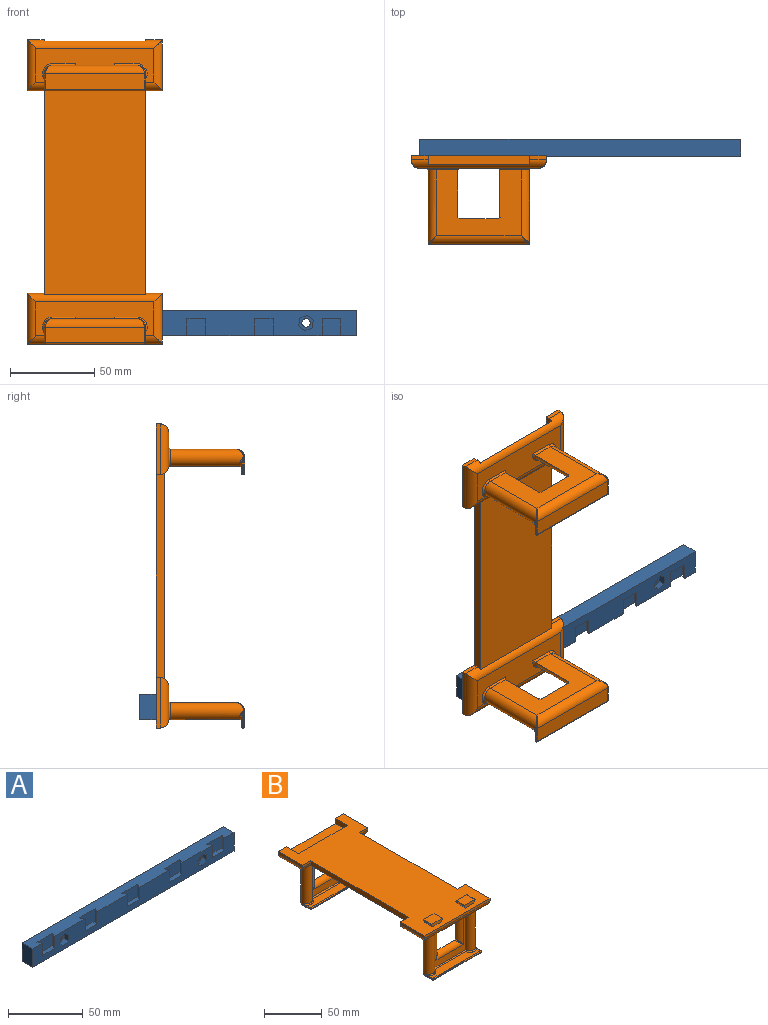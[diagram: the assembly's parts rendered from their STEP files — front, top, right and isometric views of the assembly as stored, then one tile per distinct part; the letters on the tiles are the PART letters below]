
ASSEMBLY  parts=2 mates=1
PART A: 42 faces, bbox 190x10x15 mm
  f0: plane 190x10mm, normal (0,0,1), area 1674.8mm2, adj f1,f2,f10,f13,f14,f15,f17,f18
  f1: plane 190x15mm, normal (0,-1,0), area 2189.1mm2, adj f0,f2,f3,f4,f5,f6,f7,f8
  f2: plane 15x10mm, normal (-1,0,0), area 150mm2, adj f0,f1,f3,f10
  f3: plane 190x10mm, normal (0,0,-1), area 1900mm2, adj f1,f2,f10,f24
  f4: plane 4.57x4mm, normal (-0.99,0,0.14), area 18.5mm2, adj f1,f5,f9,f12
  f5: plane 4.29x4mm, normal (-0.37,0,0.93), area 18.5mm2, adj f1,f4,f6,f12
  f6: plane 4x3.63mm, normal (0.62,0,0.79), area 18.5mm2, adj f1,f5,f7,f12
  f7: plane 4.57x4mm, normal (0.99,0,-0.14), area 18.5mm2, adj f1,f6,f8,f12
  f8: plane 4.29x4mm, normal (0.37,0,-0.93), area 18.5mm2, adj f1,f7,f9,f12
  f9: plane 4x3.63mm, normal (-0.62,0,-0.79), area 18.5mm2, adj f1,f4,f8,f12
  f10: plane 190x15mm, normal (0,1,0), area 2810.7mm2, adj f0,f2,f3,f11,f24,f31
  f11: cylinder r=2.5mm len=6mm, axis (0,1,0), area 94.2mm2, adj f10,f12
  f12: plane 9.14x8.58mm, normal (0,-1,0), area 35.8mm2, adj f4,f5,f6,f7,f8,f9,f11
  f13: plane 10x3.46mm, normal (-0.87,0.5,0), area 40mm2, adj f0,f1,f14,f16
  f14: plane 15x10mm, normal (0,-1,0), area 150mm2, adj f0,f13,f15,f16
  f15: plane 10x3.46mm, normal (0.87,0.5,0), area 40mm2, adj f0,f1,f14,f16
  f16: plane 15x3.46mm, normal (0,0,1), area 45mm2, adj f1,f13,f14,f15
  f17: plane 10x3.46mm, normal (0.87,0.5,0), area 40mm2, adj f0,f1,f19,f20
  f18: plane 10x3.46mm, normal (-0.87,0.5,0), area 40mm2, adj f0,f1,f19,f20
  f19: plane 15x10mm, normal (0,-1,0), area 150mm2, adj f0,f17,f18,f20
  f20: plane 15x3.46mm, normal (0,0,1), area 45mm2, adj f1,f17,f18,f19
  f21: plane 15x10mm, normal (0,-1,0), area 150mm2, adj f0,f22,f23,f41
  f22: plane 10x3.46mm, normal (0.87,0.5,0), area 40mm2, adj f0,f1,f21,f23
  f23: plane 15x3.46mm, normal (0,0,1), area 45mm2, adj f1,f21,f22,f41
  f24: plane 15x10mm, normal (1,0,0), area 150mm2, adj f0,f1,f3,f10
  f25: plane 4.57x4mm, normal (0.99,0,0.14), area 18.5mm2, adj f1,f26,f30,f32
  f26: plane 4.29x4mm, normal (0.37,0,0.93), area 18.5mm2, adj f1,f25,f27,f32
  f27: plane 4x3.63mm, normal (-0.62,0,0.79), area 18.5mm2, adj f1,f26,f28,f32
  f28: plane 4.57x4mm, normal (-0.99,0,-0.14), area 18.5mm2, adj f1,f27,f29,f32
  f29: plane 4.29x4mm, normal (-0.37,0,-0.93), area 18.5mm2, adj f1,f28,f30,f32
  f30: plane 4x3.63mm, normal (0.62,0,-0.79), area 18.5mm2, adj f1,f25,f29,f32
  f31: cylinder r=2.5mm len=6mm, axis (0,1,0), area 94.2mm2, adj f10,f32
  f32: plane 9.14x8.58mm, normal (0,-1,0), area 35.8mm2, adj f25,f26,f27,f28,f29,f30,f31
  f33: plane 10x3.46mm, normal (0.87,0.5,0), area 40mm2, adj f0,f1,f34,f36
  f34: plane 15x10mm, normal (0,-1,0), area 150mm2, adj f0,f33,f35,f36
  f35: plane 10x3.46mm, normal (-0.87,0.5,0), area 40mm2, adj f0,f1,f34,f36
  f36: plane 15x3.46mm, normal (0,0,1), area 45mm2, adj f1,f33,f34,f35
  f37: plane 10x3.46mm, normal (-0.87,0.5,0), area 40mm2, adj f0,f1,f39,f40
  f38: plane 10x3.46mm, normal (0.87,0.5,0), area 40mm2, adj f0,f1,f39,f40
  f39: plane 15x10mm, normal (0,-1,0), area 150mm2, adj f0,f37,f38,f40
  f40: plane 15x3.46mm, normal (0,0,1), area 45mm2, adj f1,f37,f38,f39
  f41: plane 10x3.46mm, normal (-0.87,0.5,0), area 40mm2, adj f0,f1,f21,f23
PART B: 135 faces, bbox 80.1x180.1x55.8 mm
  f0: plane 10x2.44mm, normal (0,1,0), area 24.4mm2, adj f3,f7,f12,f95
  f1: plane 10x2.44mm, normal (0,1,0), area 24.4mm2, adj f3,f23,f25,f87
  f2: plane 10x2.44mm, normal (0,-1,0), area 24.4mm2, adj f3,f5,f24,f88
  f3: plane 180x80mm, normal (0,0,1), area 10888mm2, adj f0,f1,f2,f5,f7,f11,f12,f13
  f4: plane 70x20mm, normal (0,0,-1), area 1077.8mm2, adj f86,f87,f88,f89,f97,f98,f99,f100
  f5: plane 121.41x5mm, normal (-1,0,0), area 601.2mm2, adj f2,f3,f6,f14,f88,f95
  f6: plane 121.41x60mm, normal (0,0,-1), area 7284.3mm2, adj f5,f7,f88,f95
  f7: plane 121.41x5mm, normal (1,0,0), area 601.2mm2, adj f0,f3,f6,f27,f88,f95
  f8: plane 58.6x8.3mm, normal (0,0,1), area 403.6mm2, adj f66,f70,f72,f121,f122,f123
  f9: plane 70x20mm, normal (0,0,-1), area 1077.8mm2, adj f93,f94,f95,f96,f109,f110,f111,f113
  f10: plane 41.08x40mm, normal (0,-1,0), area 453.2mm2, adj f73,f75,f90,f91,f92,f113,f122,f128
  f11: plane 30x2.44mm, normal (-1,0,0), area 73.3mm2, adj f3,f13,f14,f93
  f12: plane 30x2.44mm, normal (1,0,0), area 73.3mm2, adj f0,f3,f13,f96
  f13: plane 80x2.44mm, normal (0,-1,0), area 195.5mm2, adj f3,f11,f12,f94
  f14: plane 10x2.44mm, normal (0,1,0), area 24.4mm2, adj f3,f5,f11,f95
  f15: plane 60x5mm, normal (0,1,0), area 300mm2, adj f3,f21,f22,f23
  f16: plane 9.3x0.52mm, normal (-1,0,0), area 4.8mm2, adj f61,f65,f66,f75
  f17: plane 9.3x0.52mm, normal (1,0,0), area 4.8mm2, adj f63,f69,f72,f73
  f18: plane 50x39mm, normal (0,1,0), area 1226mm2, adj f73,f75,f76,f90,f91,f92,f109,f125
  f19: plane 58.6x9.3mm, normal (0,0,-1), area 545mm2, adj f61,f63,f64,f76
  f20: plane 58.6x0.52mm, normal (0,-1,0), area 30.5mm2, adj f64,f65,f69,f70
  f21: plane 15x5mm, normal (1,0,0), area 74.4mm2, adj f3,f15,f22,f26,f87
  f22: plane 60x14.3mm, normal (0,0,1), area 857.8mm2, adj f15,f21,f23,f87
  f23: plane 15x5mm, normal (-1,0,0), area 74.4mm2, adj f1,f3,f15,f22,f87
  f24: plane 30x2.44mm, normal (-1,0,0), area 73.3mm2, adj f2,f3,f26,f89
  f25: plane 30x2.44mm, normal (1,0,0), area 73.3mm2, adj f1,f3,f27,f86
  f26: plane 10x2.44mm, normal (0,1,0), area 24.4mm2, adj f3,f21,f24,f87
  f27: plane 10x2.44mm, normal (0,-1,0), area 24.4mm2, adj f3,f7,f25,f88
  f28: plane 41.08x40mm, normal (0,-1,0), area 453.2mm2, adj f78,f79,f83,f84,f85,f100,f104,f117
  f29: plane 50x39mm, normal (0,1,0), area 1226mm2, adj f78,f79,f81,f83,f84,f85,f97,f108
  f30: plane 58.6x8.3mm, normal (0,0,1), area 403.6mm2, adj f51,f57,f60,f116,f117,f118
  f31: plane 9.3x0.52mm, normal (-1,0,0), area 4.8mm2, adj f54,f58,f60,f78
  f32: plane 9.3x0.52mm, normal (1,0,0), area 4.8mm2, adj f49,f51,f52,f79
  f33: plane 58.6x9.3mm, normal (0,0,-1), area 545mm2, adj f49,f53,f54,f81
  f34: plane 58.6x0.52mm, normal (0,-1,0), area 30.5mm2, adj f52,f53,f57,f58
  f35: plane 10x2.54mm, normal (-0.87,0,-0.5), area 29.3mm2, adj f3,f39,f40,f41
  f36: plane 10x2.54mm, normal (0.87,0,-0.5), area 29.3mm2, adj f3,f37,f40,f41
  f37: cylinder r=0.5mm len=10mm, axis (0,1,0), area 10.5mm2, adj f36,f38,f40,f41
  f38: plane 12.67x10mm, normal (0,0,1), area 126.7mm2, adj f37,f39,f40,f41
  f39: cylinder r=0.5mm len=10mm, axis (0,1,0), area 10.5mm2, adj f35,f38,f40,f41
  f40: plane 13.67x3.29mm, normal (0,-1,0), area 40.8mm2, adj f3,f35,f36,f37,f38,f39
  f41: plane 13.67x3.29mm, normal (0,1,0), area 40.8mm2, adj f3,f35,f36,f37,f38,f39
  f42: plane 10x2.54mm, normal (-0.87,0,-0.5), area 29.3mm2, adj f3,f46,f47,f48
  f43: plane 10x2.54mm, normal (0.87,0,-0.5), area 29.3mm2, adj f3,f44,f47,f48
  f44: cylinder r=0.5mm len=10mm, axis (0,1,0), area 10.5mm2, adj f43,f45,f47,f48
  f45: plane 12.67x10mm, normal (0,0,1), area 126.7mm2, adj f44,f46,f47,f48
  f46: cylinder r=0.5mm len=10mm, axis (0,1,0), area 10.5mm2, adj f42,f45,f47,f48
  f47: plane 13.67x3.29mm, normal (0,-1,0), area 40.8mm2, adj f3,f42,f43,f44,f45,f46
  f48: plane 13.67x3.29mm, normal (0,1,0), area 40.8mm2, adj f3,f42,f43,f44,f45,f46
  f49: cylinder r=0.7mm len=9.3mm, axis (0,1,0), area 10.2mm2, adj f32,f33,f50,f82
  f50: sphere r=0.7mm, area 0.8mm2, adj f49,f52,f53
  f51: cylinder r=0.7mm len=9.3mm, axis (0,-1,0), area 7.9mm2, adj f30,f32,f55,f115
  f52: cylinder r=0.7mm len=0.7mm, axis (0,0,1), area 0.6mm2, adj f32,f34,f50,f55
  f53: cylinder r=0.7mm len=58.6mm, axis (1,0,0), area 64.4mm2, adj f33,f34,f50,f56
  f54: cylinder r=0.7mm len=9.3mm, axis (0,1,0), area 10.2mm2, adj f31,f33,f56,f80
  f55: sphere r=0.7mm, area 0.8mm2, adj f51,f52,f57
  f56: sphere r=0.7mm, area 0.8mm2, adj f53,f54,f58
  f57: cylinder r=0.7mm len=58.6mm, axis (-1,0,0), area 64.4mm2, adj f30,f34,f55,f59
  f58: cylinder r=0.7mm len=0.7mm, axis (0,0,-1), area 0.6mm2, adj f31,f34,f56,f59
  f59: sphere r=0.7mm, area 0.8mm2, adj f57,f58,f60
  f60: cylinder r=0.7mm len=9.3mm, axis (0,-1,0), area 7.9mm2, adj f30,f31,f59,f119
  f61: cylinder r=0.7mm len=9.3mm, axis (0,1,0), area 10.2mm2, adj f16,f19,f62,f77
  f62: sphere r=0.7mm, area 0.8mm2, adj f61,f64,f65
  f63: cylinder r=0.7mm len=9.3mm, axis (0,1,0), area 10.2mm2, adj f17,f19,f67,f74
  f64: cylinder r=0.7mm len=58.6mm, axis (-1,0,0), area 64.4mm2, adj f19,f20,f62,f67
  f65: cylinder r=0.7mm len=0.7mm, axis (0,0,1), area 0.6mm2, adj f16,f20,f62,f68
  f66: cylinder r=0.7mm len=9.3mm, axis (0,-1,0), area 7.9mm2, adj f8,f16,f68,f124
  f67: sphere r=0.7mm, area 0.8mm2, adj f63,f64,f69
  f68: sphere r=0.7mm, area 0.8mm2, adj f65,f66,f70
  f69: cylinder r=0.7mm len=0.7mm, axis (0,0,-1), area 0.6mm2, adj f17,f20,f67,f71
  f70: cylinder r=0.7mm len=58.6mm, axis (1,0,0), area 64.4mm2, adj f8,f20,f68,f71
  f71: sphere r=0.7mm, area 0.8mm2, adj f69,f70,f72
  f72: cylinder r=0.7mm len=9.3mm, axis (0,-1,0), area 7.9mm2, adj f8,f17,f71,f120
  f73: cylinder r=5mm len=43.3mm, axis (0,0,1), area 975.6mm2, adj f10,f17,f18,f74,f120,f121,f127,f129
  f74: bspline ~5.19x5mm, area 3.8mm2, adj f63,f73,f76
  f75: cylinder r=5mm len=43.3mm, axis (0,0,-1), area 975.6mm2, adj f10,f16,f18,f77,f110,f112,f114,f123
  f76: cylinder r=5mm len=58.6mm, axis (1,0,0), area 426.5mm2, adj f18,f19,f74,f77
  f77: bspline ~5.19x5mm, area 3.8mm2, adj f61,f75,f76
  f78: cylinder r=5mm len=43.3mm, axis (0,0,1), area 975.6mm2, adj f28,f29,f31,f80,f103,f105,f107,f118
  f79: cylinder r=5mm len=43.3mm, axis (0,0,-1), area 975.6mm2, adj f28,f29,f32,f82,f99,f101,f102,f115
  f80: bspline ~5.19x5mm, area 3.8mm2, adj f54,f78,f81
  f81: cylinder r=5mm len=58.6mm, axis (-1,0,0), area 426.5mm2, adj f29,f33,f80,f82
  f82: bspline ~5.19x5mm, area 3.8mm2, adj f49,f79,f81
  f83: cylinder r=5mm len=34mm, axis (0,0,1), area 243.5mm2, adj f28,f29,f106,f132
  f84: cylinder r=5mm len=35mm, axis (-1,0,0), area 227.8mm2, adj f28,f29,f131,f132
  f85: cylinder r=5mm len=34mm, axis (0,0,-1), area 243.5mm2, adj f28,f29,f98,f131
  f86: cylinder r=5mm len=30mm, axis (0,-1,0), area 196.3mm2, adj f4,f25,f87,f88
  f87: cylinder r=5mm len=80mm, axis (1,0,0), area 428.1mm2, adj f1,f4,f21,f22,f23,f26,f86,f89
  f88: cylinder r=5mm len=80mm, axis (-1,0,0), area 420.5mm2, adj f2,f4,f5,f6,f7,f27,f86,f89
  f89: cylinder r=5mm len=30mm, axis (0,-1,0), area 196.3mm2, adj f4,f24,f87,f88
  f90: cylinder r=5mm len=34mm, axis (0,0,1), area 243.5mm2, adj f10,f18,f126,f133
  f91: cylinder r=5mm len=35mm, axis (1,0,0), area 227.8mm2, adj f10,f18,f133,f134
  f92: cylinder r=5mm len=34mm, axis (0,0,-1), area 243.5mm2, adj f10,f18,f111,f134
  f93: cylinder r=5mm len=30mm, axis (0,1,0), area 196.3mm2, adj f9,f11,f94,f95
  f94: cylinder r=5mm len=80mm, axis (-1,0,0), area 581.5mm2, adj f9,f13,f93,f96,f112,f129
  f95: cylinder r=5mm len=80mm, axis (1,0,0), area 428.1mm2, adj f0,f5,f6,f7,f9,f14,f93,f96
  f96: cylinder r=5mm len=30mm, axis (0,1,0), area 196.3mm2, adj f9,f12,f94,f95
  f97: plane 13.49x1.07mm, normal (0,0.71,-0.71), area 18.3mm2, adj f4,f29,f98,f99
  f98: cone r=6mm half-angle=45deg, axis (0,0,1), area 12.9mm2, adj f4,f85,f97,f100
  f99: cone r=6mm half-angle=45deg, axis (0,0,1), area 19.9mm2, adj f4,f79,f97,f101
  f100: plane 2.57x1.07mm, normal (0,-0.71,-0.71), area 2.9mm2, adj f4,f28,f98,f102
  f101: bspline ~6.63x1.67mm, area 8.5mm2, adj f79,f88,f99,f102
  f102: cone r=6mm half-angle=45deg, axis (0,0,1), area 7mm2, adj f4,f79,f100,f101
  f103: cone r=6mm half-angle=45deg, axis (0,0,1), area 7mm2, adj f4,f78,f104,f105
  f104: plane 2.57x1.07mm, normal (0,-0.71,-0.71), area 2.9mm2, adj f4,f28,f103,f106
  f105: bspline ~6.63x1.67mm, area 8.5mm2, adj f78,f88,f103,f107
  f106: cone r=6mm half-angle=45deg, axis (0,0,1), area 12.9mm2, adj f4,f83,f104,f108
  f107: cone r=6mm half-angle=45deg, axis (0,0,1), area 19.9mm2, adj f4,f78,f105,f108
  f108: plane 13.49x1.07mm, normal (0,0.71,-0.71), area 18.3mm2, adj f4,f29,f106,f107
  f109: plane 13.49x1.07mm, normal (0,0.71,-0.71), area 18.3mm2, adj f9,f18,f110,f111
  f110: cone r=6mm half-angle=45deg, axis (0,0,1), area 19.9mm2, adj f9,f75,f109,f112
  f111: cone r=6mm half-angle=45deg, axis (0,0,1), area 12.9mm2, adj f9,f92,f109,f113
  f112: bspline ~6.63x1.67mm, area 8.5mm2, adj f75,f94,f110,f114
  f113: plane 2.57x1.07mm, normal (0,-0.71,-0.71), area 2.9mm2, adj f9,f10,f111,f114
  f114: cone r=6mm half-angle=45deg, axis (0,0,1), area 7mm2, adj f9,f75,f112,f113
  f115: bspline ~4.18x1.7mm, area 2mm2, adj f51,f79,f116
  f116: cone r=6mm half-angle=45deg, axis (0,0,-1), area 17.8mm2, adj f30,f79,f115,f117
  f117: plane 40.07x1.07mm, normal (0,-0.71,0.71), area 55.2mm2, adj f28,f30,f116,f118
  f118: cone r=6mm half-angle=45deg, axis (0,0,-1), area 17.8mm2, adj f30,f78,f117,f119
  f119: bspline ~4.18x1.7mm, area 2mm2, adj f60,f78,f118
  f120: bspline ~4.18x1.7mm, area 2mm2, adj f72,f73,f121
  f121: cone r=6mm half-angle=45deg, axis (0,0,-1), area 17.8mm2, adj f8,f73,f120,f122
  f122: plane 40.07x1.07mm, normal (0,-0.71,0.71), area 55.2mm2, adj f8,f10,f121,f123
  f123: cone r=6mm half-angle=45deg, axis (0,0,-1), area 17.8mm2, adj f8,f75,f122,f124
  f124: bspline ~4.18x1.7mm, area 2mm2, adj f66,f75,f123
  f125: plane 13.49x1.07mm, normal (0,0.71,-0.71), area 18.3mm2, adj f9,f18,f126,f127
  f126: cone r=6mm half-angle=45deg, axis (0,0,1), area 12.9mm2, adj f9,f90,f125,f128
  f127: cone r=6mm half-angle=45deg, axis (0,0,1), area 19.9mm2, adj f9,f73,f125,f129
  f128: plane 2.57x1.07mm, normal (0,-0.71,-0.71), area 2.9mm2, adj f9,f10,f126,f130
  f129: bspline ~6.63x1.67mm, area 8.5mm2, adj f73,f94,f127,f130
  f130: cone r=6mm half-angle=45deg, axis (0,0,1), area 7mm2, adj f9,f73,f128,f129
  f131: bspline ~6.12x6.12mm, area 5.1mm2, adj f29,f84,f85
  f132: bspline ~6.12x6.12mm, area 5.1mm2, adj f29,f83,f84
  f133: bspline ~6.12x6.12mm, area 5.1mm2, adj f18,f90,f91
  f134: bspline ~6.12x6.12mm, area 5.1mm2, adj f18,f91,f92
PLACE A rot(axis=(0,1,0),180deg) t=(37.01,-78.18,56.72)mm
PLACE B rot(axis=(0,0.71,0.71),180deg) t=(-1.78,-90.04,51.72)mm
MATE fastened B.f48 <-> A.f40  axis (0,0,1) through (-42.99,-86.36,51.72)mm
